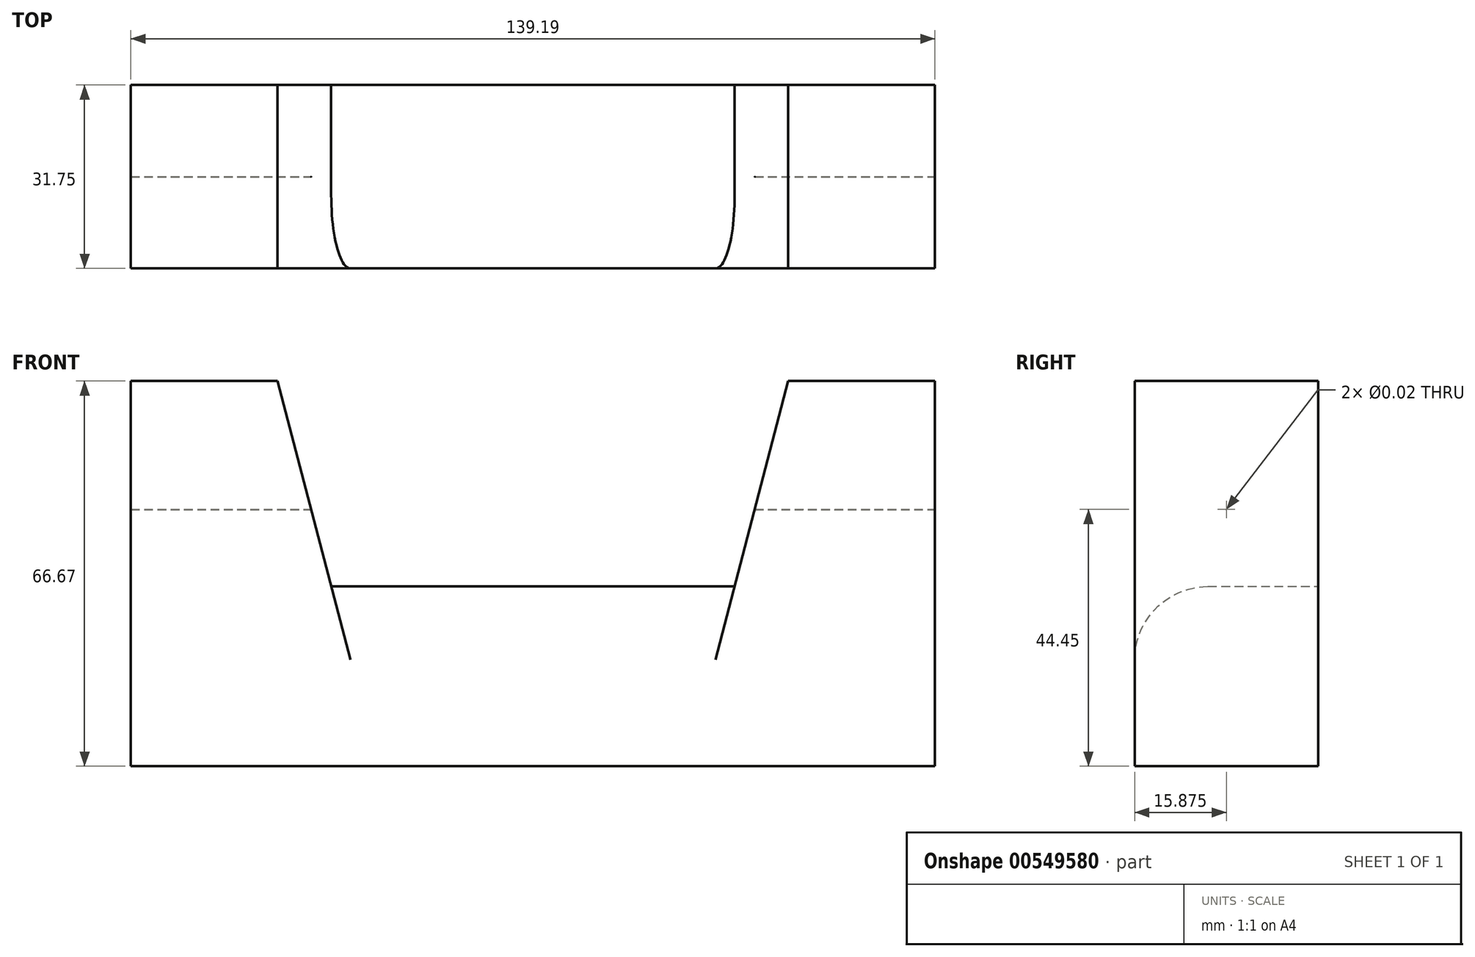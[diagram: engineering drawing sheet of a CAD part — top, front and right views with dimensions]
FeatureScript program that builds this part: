
annotation { "Feature Type Name" : "Feature", "Feature Type Description" : "" }
export const myFeature = defineFeature(function(context is Context, id is Id, definition is map)
    precondition{}
    {
        {
            var Q0;
            Q0=qCreatedBy(makeId("Front.planeOp"),FACE);
            var sketch = newSketch(context, id + "F0", { "sketchPlane" : qUnion([Q0])});
            skLineSegment(sketch, "E0", {"start": v(0, 0) * mm, "end": v(0, 66.68) * mm});
            skLineSegment(sketch, "E1", {"start": v(0, 66.68) * mm, "end": v(25.4, 66.68) * mm});
            skLineSegment(sketch, "E2", {"start": v(25.4, 66.67) * mm, "end": v(34.67, 31.11) * mm});
            skLineSegment(sketch, "E3", {"start": v(34.67, 31.11) * mm, "end": v(104.52, 31.12) * mm});
            skLineSegment(sketch, "E4", {"start": v(104.52, 31.12) * mm, "end": v(113.8, 66.67) * mm});
            skLineSegment(sketch, "E5", {"start": v(113.8, 66.68) * mm, "end": v(139.2, 66.68) * mm});
            skLineSegment(sketch, "E6", {"start": v(139.2, 66.67) * mm, "end": v(139.2, 0) * mm});
            skLineSegment(sketch, "E7", {"start": v(139.2, 0) * mm, "end": v(0, 0) * mm});
            skSolve(sketch);
        }
        {
            var Q0;
            Q0=makeQuery(id+"F0.imprint","IMPRINT",FACE,{"disambiguationData":[TD([[makeQuery(id+"F0.imprint","IMPRINT",EDGE,{"derivedFrom":sQuery(id+"F0.wireOp",EDGE,"E0")}),-1.0]])]});
            extrude(context, id + "F1", {"entities" : qUnion([Q0]), "depth" : 31.75 * mm, "offsetDistance" : 25.4 * mm});
        }
        {
            var Q0;
            Q0=makeQuery(id+"F1.opExtrude","SWEPT_FACE",FACE,{"disambiguationData":[OSD([sQuery(id+"F0.wireOp",EDGE,"E6")])]});
            var sketch = newSketch(context, id + "F2", { "sketchPlane" : qUnion([Q0])});
            skPoint(sketch, "E8", {"position": v(-15.88, 44.45) * mm});
            skPoint(sketch, "E8.positionSnap0", {"position": v(-15.88, 66.67) * mm});
            skSolve(sketch);
        }
        {
            var Q0;
            Q0=sQuery(id+"F2.wireOp",VERTEX,"E8");
            var Q1;
            Q1=makeQuery(id+"F1.opExtrude","SWEPT_BODY",BODY,{"disambiguationData":[OSD([sQuery(id+"F0.wireOp",EDGE,"E0"),sQuery(id+"F0.wireOp",EDGE,"E1"),sQuery(id+"F0.wireOp",EDGE,"E2"),sQuery(id+"F0.wireOp",EDGE,"E3"),sQuery(id+"F0.wireOp",EDGE,"E4"),sQuery(id+"F0.wireOp",EDGE,"E5"),sQuery(id+"F0.wireOp",EDGE,"E6"),sQuery(id+"F0.wireOp",EDGE,"E7")])]});
            hole(context, id + "F3", {"style" : HoleStyle.SIMPLE, "endStyle" : HoleEndStyle.THROUGH, "standardTappedOrClearance" : lookupTablePath({ "standard" : "ANSI", "size" : "9/16 (0.56)", "type" : "Drilled" }), "standardBlindInLast" : lookupTablePath({ "standard" : "ANSI", "size" : "9/16", "type" : "Drilled" }), "holeDiameter" : 9 / 406.4 * mm, "isTappedThrough" : true, "tappedDepth" : 12.7 * mm, "tapClearance" : 3, "startFromSketch" : true, "locations" : qUnion([Q0]), "scope" : qUnion([Q1])});
        }
        {
            var Q0;
            Q0=makeQuery(id+"F1.opExtrude","CAP_EDGE",EDGE,{"disambiguationData":[OSD([sQuery(id+"F0.wireOp",EDGE,"E3")])],"isStart":false});
            fillet(context, id + "F4", {"entities" : qUnion([Q0]), "radius" : 12.7 * mm, "tangentPropagation" : true, "allowEdgeOverflow" : false});
        }
    });
